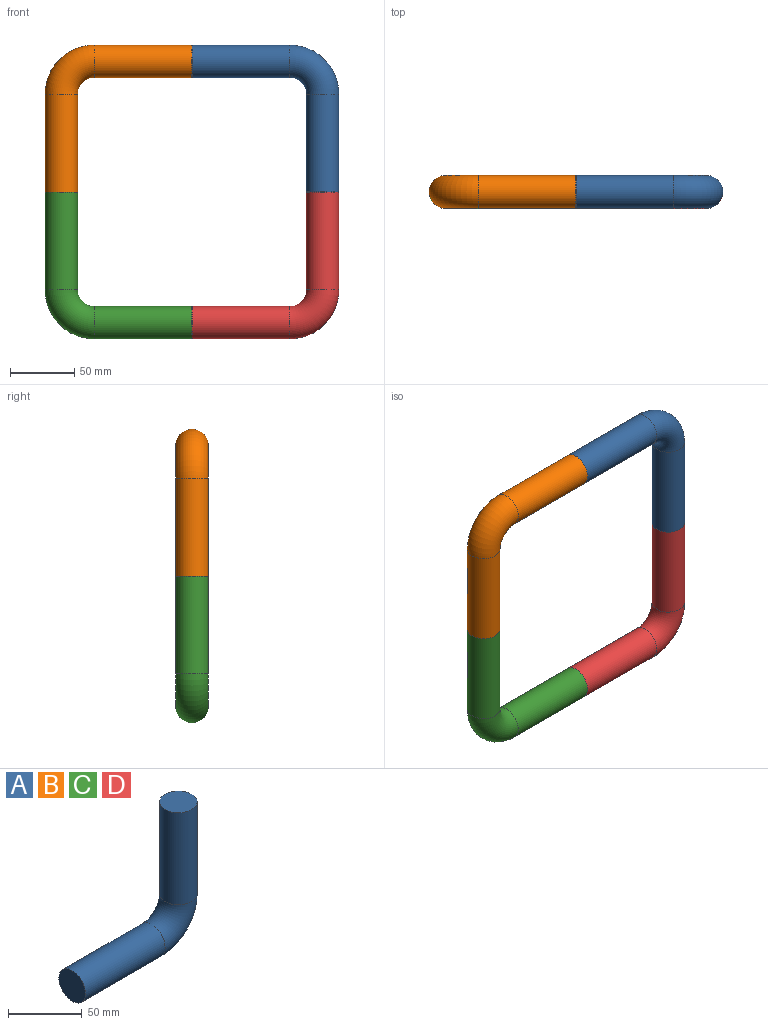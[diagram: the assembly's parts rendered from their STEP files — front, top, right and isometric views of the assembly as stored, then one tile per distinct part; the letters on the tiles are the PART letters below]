
ASSEMBLY  parts=4 mates=4
PART A: 5 faces, bbox 117.4x25.4x117.4 mm
  f0: plane 25.4x25.4mm, normal (0,0,1), area 506.7mm2, adj f2
  f1: plane 25.4x25.4mm, normal (-1,0,0), area 506.7mm2, adj f4
  f2: cylinder r=12.7mm len=76.2mm, axis (0,0,-1), area 6080.5mm2, adj f0,f3
  f3: torus R=25.4mm, axis (0,1,0), area 3183.7mm2, adj f2,f4
  f4: cylinder r=12.7mm len=76.2mm, axis (-1,0,0), area 6080.5mm2, adj f1,f3
PART B: same geometry as A
PART C: same geometry as A
PART D: same geometry as A
PLACE A rot(axis=(1,0,0),180deg) t=(-200.64,-161.64,106.55)mm
PLACE B rot(axis=(-0.71,0,-0.71),180deg) t=(-378.44,-161.64,81.15)mm
PLACE C rot(axis=(0,0,1),180deg) t=(-353.04,-161.64,-96.65)mm
PLACE D t=(-200.64,-161.64,-96.65)mm
MATE planar A.f2 <-> D.f2  axis (0,0,-1) through (-175.24,-161.64,4.95)mm
MATE planar C.f4 <-> D.f4  axis (1,0,0) through (-276.84,-161.64,-96.65)mm
MATE planar B.f4 <-> C.f2  axis (0,0,-1) through (-378.44,-161.64,4.95)mm
MATE planar B.f2 <-> C.f2  axis (-1,0,0) through (-276.84,-161.64,106.55)mm
